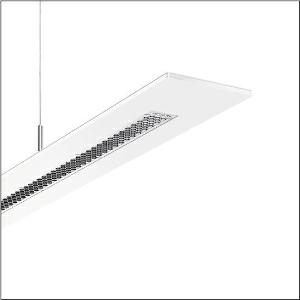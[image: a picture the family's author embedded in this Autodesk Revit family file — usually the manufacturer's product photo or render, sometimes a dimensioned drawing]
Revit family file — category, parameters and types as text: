
# Revit family: arktika_r__21_duo_5mb252dl60830_d82e
name_source: partatom
category: Lighting Fixtures
units: mm (PartAtom-declared; Revit-internal decimal feet)

## family parameters
Cut with Voids When Loaded = No
Host = Face
Light Source = No
Part Type = Normal
Room Calculation Point = No
Round Connector Dimension = Use Diameter
Shared = No

## types (1)
- --- (1 x LED 3000K / CRI = 80 (unbekannt), 8100 lm, 3000K)
    Apparent Load = 67 VA
    CIE Flux Codes = 81 100 100 79 100
    Color Rendering = 80
    Color Temperature = 3000K
    Default Elevation = 1800 mm
    Description = Arktika® 21 duo, office luminaire, primary anti-glare with honeycomb louvre, of plastic, aluminium vaporised, highly specular, light emission: direct/indirect distribution, primary light characteristic: symmetric, installation type: suspended mounting, LED, rated luminous flux: 8.100lm, luminous efficacy: 122lm/W, light colour: 830, colour temperature: 3000K, control gear: ECG DALI, with terminal, 3+2-pole, max. 2.5mm², mains connection: 220..240V, AC, 50/60Hz, rated input power: 67W, housing, of aluminium, powder-coated, traffic white (RAL 9016), 2-length, length: 2.280mm, width: 120mm, height: 8mm, protection rating (complete): IP20, insulation class (complete): insulation class II (safety insulation), certification: CE, packaging unit: 1 piece
    Height = 8 mm  [stored 0.0262467 ft]
    Lamp = 1 x LED 3000K / CRI >= 80 (unbekannt)
    Lamp Light Flux = 8100 lm
    Lamp count = 1
    Length = 2280 mm
    Luminous efficacy = 122 lm/W
    Manufacturer = Siteco
    ModVariant = No
    Model = 5MB252DL60830
    Mounting Place = Ceiling
    Mounting Type = Pendant
    Number of Poles = 1
    OnlyDefault = Yes
    Power Factor = 1
    Product Name = Arktika® 21 duo
    Product group = office luminaire | ceiling pendant
    ProductGroupID = 902
    Protection Class = Protection class II
    Protection Degree = IP 20
    RLX_Detail_Level = 1
    RLX_Emergency_Light_Flux = 0 lm
    RLX_Emergency_Type = 0
    RLX_Emergency_Type_DB = No
    RlxData = <blob elided: 39801 chars, md5=46da2ac2>
    Socket = socket
    Standby Power = 0 W
    System Light Flux = 8100 lm
    System Power = 67 W
    Type Comments = factory setting: luminous flux: 100 % | dim-lin: 254 | 1330 mA
    Type Image = l_1006128.jpg
    URL = http://relux.com
    VarID = @adj_148813
    Voltage = 0 V
    Weight = 0.00 kg
    Width = 120 mm

note: [stored X ft] marks values corroborated as IEEE doubles in the binary element streams (Revit-internal decimal feet)

## geometry (parser evidence)
native form markers: Blend x4, Sweep x12
no freeform markers — native parametric forms only
